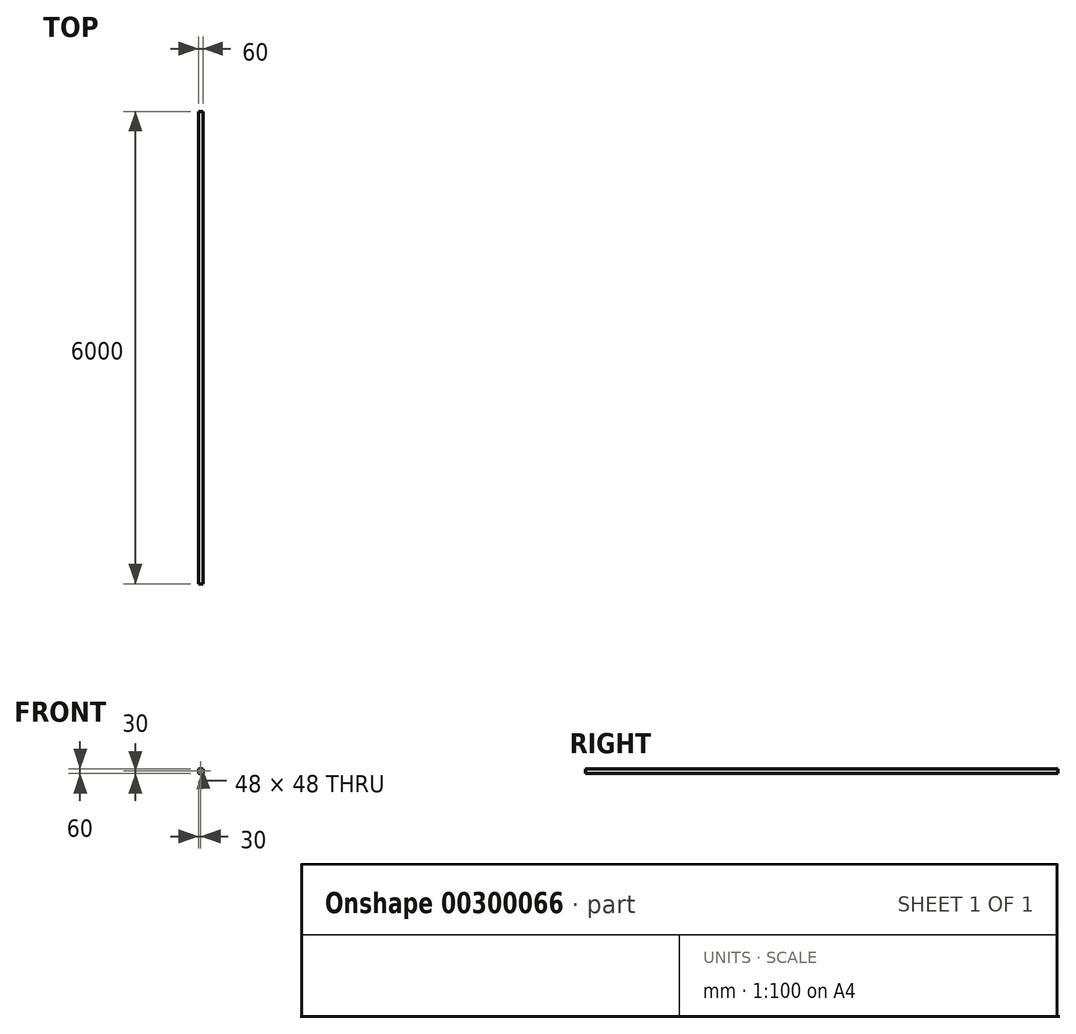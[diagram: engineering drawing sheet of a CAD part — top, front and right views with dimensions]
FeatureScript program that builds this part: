
annotation { "Feature Type Name" : "Feature", "Feature Type Description" : "" }
export const myFeature = defineFeature(function(context is Context, id is Id, definition is map)
    precondition{}
    {
        {
            var Q0;
            Q0=qCreatedBy(makeId("Front.planeOp"),FACE);
            var sketch = newSketch(context, id + "F0", { "sketchPlane" : qUnion([Q0])});
            skLineSegment(sketch, "E0.bottom", {"start": v(-30, -30) * mm, "end": v(30, -30) * mm});
            skLineSegment(sketch, "E0.top", {"start": v(-30, 30) * mm, "end": v(30, 30) * mm});
            skLineSegment(sketch, "E0.left", {"start": v(-30, -30) * mm, "end": v(-30, 30) * mm});
            skLineSegment(sketch, "E0.right", {"start": v(30, -30) * mm, "end": v(30, 30) * mm});
            skPoint(sketch, "E0.middle", {"position": v(0, 0) * mm});
            skLineSegment(sketch, "E1.bottom", {"start": v(-24, -24) * mm, "end": v(24, -24) * mm});
            skLineSegment(sketch, "E1.top", {"start": v(-24, 24) * mm, "end": v(24, 24) * mm});
            skLineSegment(sketch, "E1.left", {"start": v(-24, -24) * mm, "end": v(-24, 24) * mm});
            skLineSegment(sketch, "E1.right", {"start": v(24, -24) * mm, "end": v(24, 24) * mm});
            skSolve(sketch);
        }
        {
            var Q0;
            Q0 = qSketchRegion(id + "F0", true);
            extrude(context, id + "F1", {"entities" : qUnion([Q0]), "depth" : 6000 * mm});
        }
    });
